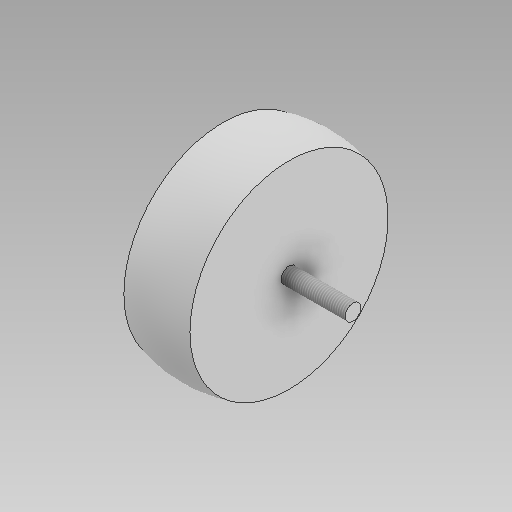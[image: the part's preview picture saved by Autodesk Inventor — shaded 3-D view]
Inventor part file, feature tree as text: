
AUTODESK INVENTOR PART (.ipt)
format: ipt  version: 2021.2 (Build 252289000, 289)  size: 118,272 bytes
history: native  units: in
note: dims shown in document units (in); Inventor stores cm internally (conversion verified against a paired STEP export)
features: sketch x3, other x1, revolve x1, extrude x1, thread x1
ambient origin geometry x8: Origin, YZ Plane, XZ Plane, XY Plane, X Axis, Y Axis, Z Axis, Center Point
bodies: Body1 (feature_tree)
feature tree (7):
  other  "ソリッド1"
  revolve  "回転1"
  sketch  "スケッチ3"
  extrude  "押し出し1"  Depth=3.0906in
  thread  "ねじ1"
  sketch  "スケッチ2"
  sketch  "スケッチ4"
